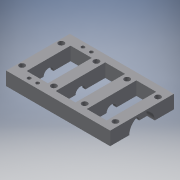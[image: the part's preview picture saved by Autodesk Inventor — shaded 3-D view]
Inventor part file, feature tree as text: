
AUTODESK INVENTOR PART (.ipt)
format: ipt  version: 2017 SP1 (Build 210196100, 196)  size: 249,344 bytes
history: native  units: mm
features: extrude x12, sketch x12, reference x4, other x4, projected_geometry x1
ambient origin geometry x8: Origin, YZ Plane, XZ Plane, XY Plane, X Axis, Y Axis, Z Axis, Center Point
bodies: Solid1 (feature_tree)
feature tree (33):
  extrude  "Extrusion1"  Depth=28.0mm
  extrude  "Extrusion2"  Depth=70.0mm
  extrude  "Extrusion3"  Depth=15.0mm
  extrude  "Extrusion4"  Depth=14.0mm
  extrude  "Extrusion5"  Depth=15.0mm
  extrude  "Extrusion6"  Depth=11.0mm
  extrude  "Extrusion7"  Depth=11.0mm
  extrude  "Extrusion8"  Depth=11.0mm
  extrude  "Extrusion9"  Depth=60.0mm
  extrude  "Extrusion10"  Depth=8.0mm
  extrude  "Extrusion11"  Depth=10.0mm TaperAngle=0.0deg
  extrude  "Extrusion12"  Depth=15.0mm
  sketch  "Sketch1"  dims[d0=16.0mm d1=28.0mm]
  sketch  "Sketch2"  dims[d2=28.0mm d3=70.0mm]
  sketch  "Sketch3"  dims[d4=10.0mm d5=15.0mm]
  sketch  "Sketch4"  dims[d6=19.0mm d7=0.0mm d8=14.0mm]
  sketch  "Sketch5"  dims[d9=15.0mm d10=0.0mm d11=36.0mm]
  sketch  "Sketch6"  dims[d12=11.0mm d13=0.0mm d14=35.0mm]
  sketch  "Sketch7"  dims[d15=11.0mm d16=0.0mm d17=35.0mm]
  sketch  "Sketch8"  dims[d18=11.0mm d19=0.0mm d20=35.0mm]
  sketch  "Sketch9"  dims[d21=7.0mm d22=0.0mm d23=60.0mm]
  sketch  "Sketch10"  dims[d24=8.0mm d25=7.5mm]
  projected_geometry  "Projected Loop1"
  sketch  "Sketch11"  dims[d26=87.0mm d27=10.0mm d28=0.0mm]
  reference  "Reference1"
  reference  "Reference2"
  reference  "Reference3"
  reference  "Reference4"
  sketch  "Sketch12"  dims[d29=14.0mm d30=15.0mm d31=30.0mm d32=10.0mm d33=0.0mm d34=35.0mm d35=11.0mm d36=0.0mm d37=8.0mm d38=10.0mm d39=10.0mm d40=0.0mm d41=31.0mm d42=10.0mm d43=0.0mm d44=10.0mm d45=0.0mm]
  other  "<userpath>\Documents\st motor\two cylinder solenoid valve\engine.iam"
  other  "engine.iam"
  other  "hall follower:1"
  other  "hall follower:2"
